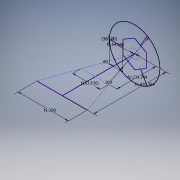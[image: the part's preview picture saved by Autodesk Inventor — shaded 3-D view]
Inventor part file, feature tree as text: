
AUTODESK INVENTOR PART (.ipt)
format: ipt  version: 2016 (Build 200138000, 138)  size: 97,792 bytes
history: native  units: mm
features: sketch x2
ambient origin geometry x8: Origin, YZ Plane, XZ Plane, XY Plane, X Axis, Y Axis, Z Axis, Center Point
feature tree (2):
  sketch  "Sketch1"  dims[d1=30.0mm d3=360.0deg]
  sketch  "Sketch2"  dims[d5=80.0mm d6=430.364mm d7=300.0mm d8=234.744mm d11=54.545455mm]
